# Revit family: НЕВАТОМ_Щит приточно-вытяжной вентиляцией ABUm-PE-1-ZM, Версия 1
name_source: partatom
category: Электрооборудование
revit_build: Autodesk Revit 2017 (Build: 20170118_1100(x64)
units: mm (PartAtom-declared; Revit-internal decimal feet)

## family parameters
Всегда вертикально = Да
Конфигурация панели = Два столбца, слева направо
На основе рабочей плоскости = Нет
Общий = Нет
При загрузке вырезать с полостями = Нет
Размер круглого соединителя = Использовать диаметр
Тип детали = Щит
Точка расчета площади = Нет

## types (26) — shared parameters
ADSK_Единица измерения = шт.
ADSK_Завод-изготовитель = НЕВАТОМ
ADSK_Количество = 1
ADSK_Напряжение = 380 В

## per-type parameters (varying)
| type | ADSK_Размер_Высота | ADSK_Размер_Длина | ADSK_Размер_Ширина | НЕВАТОМ_Количество ступеней нагревателя | НЕВАТОМ_Максимальная мощность нагревателя | НЕВАТОМ_Номинальный ток двигателя | НЕВАТОМ_Ориентировочная мощность двигателя | НЕВАТОМ_Преобразователь частоты Danfoss, кВт |
| ABUm-РE-1-ZM-0,35/0,35-4,5/1 | 800 мм | 680 мм | 200 мм | 1 | 5 кВт | 2 А | 0 кВт | ND-051 0,37 кВт для 3 фазы |
| ABUm-РE-1-ZM-0,75/0,75-4,5/1 | 800 мм | 680 мм | 200 мм | 1 | 5 кВт | 3 А | 1 кВт | ND-051 0,75 кВт для 3 фазы |
| ABUm-РE-1-ZM-0,35/0,35-6/1 | 800 мм | 680 мм | 200 мм | 1 | 6 кВт | 2 А | 0 кВт | ND-051 0,37 кВт для 3 фазы |
| ABUm-РE-1-ZM-0,75/0,75-6/1 | 800 мм | 680 мм | 200 мм | 1 | 6 кВт | 3 А | 1 кВт | ND-051 0,75 кВт для 3 фазы |
| ABUm-РE-1-ZM-0,35/0,35-7,5/1 | 800 мм | 680 мм | 200 мм | 0 | 0 кВт | 0 А | 0 кВт |  |
| ABUm-РE-1-ZM-0,75/0,75-7,5/1 | 800 мм | 680 мм | 200 мм | 1 | 8 кВт | 3 А | 1 кВт | ND-051 0,75 кВт для 3 фазы |
| ABUm-РE-1-ZM-0,35/0,35-12/2 | 800 мм | 680 мм | 200 мм | 2 | 12 кВт | 2 А | 0 кВт | ND-051 0,37 кВт для 3 фазы |
| ABUm-РE-1-ZM-0,75/0,75-12/2 | 800 мм | 680 мм | 200 мм | 2 | 12 кВт | 3 А | 1 кВт | ND-051 0,75 кВт для 3 фазы |
| ABUm-РE-1-ZM-0,35/0,35-15/2 | 800 мм | 680 мм | 200 мм | 0 | 0 кВт | 0 А | 0 кВт | ND-051 0,37 кВт для 3 фазы |
| ABUm-РE-1-ZM-0,75/0,75-15/2 | 800 мм | 680 мм | 200 мм | 0 | 0 кВт | 0 А | 0 кВт | ND-051 0,75 кВт для 3 фазы |
| ABUm-РE-1-ZM-0,75/0,75-22,5/2 | 800 мм | 680 мм | 200 мм | 2 | 23 кВт | 3 А | 1 кВт | ND-051 0,75 кВт для 3 фазы |
| ABUm-РE-1-ZM-1,5/1,5-22,5/2 | 800 мм | 680 мм | 200 мм | 2 | 23 кВт | 4 А | 2 кВт | ND-051 1,5 кВт для 3 фазы |
| ABUm-РE-1-ZM-1,5/1,5-30/2 | 800 мм | 680 мм | 200 мм | 2 | 30 кВт | 4 А | 2 кВт | ND-051 1,5 кВт для 3 фазы |
| ABUm-РE-1-ZM-2,2/2,2-30/2 | 800 мм | 680 мм | 200 мм | 2 | 30 кВт | 6 А | 2 кВт | ND-051 2,2 кВт для 3 фазы |
| ABUm-РE-1-ZM-1,5/1,5-37,5/3 | 800 мм | 680 мм | 200 мм | 3 | 38 кВт | 4 А | 2 кВт | ND-051 1,5 кВт для 3 фазы |
| ABUm-РE-1-ZM-2,2/2,2-37,5/3 | 800 мм | 680 мм | 200 мм | 3 | 38 кВт | 6 А | 2 кВт | ND-051 2,2 кВт для 3 фазы |
| ABUm-РE-1-ZM-2,2/2,2-45/3 | 800 мм | 680 мм | 200 мм | 3 | 45 кВт | 6 А | 2 кВт | ND-051 2,2 кВт для 3 фазы |
| ABUm-РE-1-ZM-4,0/4,0-45/3 | 800 мм | 680 мм | 200 мм | 3 | 0 кВт | 0 А | 0 кВт | ND-051 4,0 кВт для 3 фазы |
| ABUm-РE-1-ZM-4,0/4,0-60/4 | 800 мм | 680 мм | 200 мм | 4 | 60 кВт | 10 А | 4 кВт | ND-051 4,0 кВт для 3 фазы |
| ABUm-РE-1-ZM-4,0/4,0-75/5 | 1000 мм | 880 мм | 300 мм | 5 | 75 кВт | 10 А | 4 кВт | ND-051 4,0 кВт для 3 фазы |
| ABUm-РE-1-ZM-5,5/5,5-75/5 | 1000 мм | 880 мм | 300 мм | 0 | 0 кВт | 0 А | 0 кВт | ND-051 5,5 кВт для 3 фазы |
| ABUm-РE-1-ZM-5,5/5,5-90/5 | 1000 мм | 880 мм | 300 мм | 5 | 90 кВт | 13 А | 6 кВт | ND-051 5,5 кВт для 3 фазы |
| ABUm-РE-1-ZM-7,5/7,5-90/5 | 1000 мм | 880 мм | 300 мм | 5 | 90 кВт | 18 А | 8 кВт | ND-051 7,5 кВт для 3 фазы |
| ABUm-РE-1-ZM-7,5/7,5-120/5 | 1000 мм | 880 мм | 300 мм | 5 | 120 кВт | 18 А | 8 кВт | ND-051 7,5 кВт для 3 фазы |
| ABUm-РE-1-ZM-15/15-120/5 | 1000 мм | 880 мм | 300 мм | 5 | 120 кВт | 32 А | 15 кВт | ND-051 15 кВт для 3 фазы |
| ABUm-РE-1-ZM-5,5/5,5-60/4 | 800 мм | 680 мм | 200 мм | 4 | 60 кВт | 13 А | 6 кВт | ND-051 5,5 кВт для 3 фазы |

note: column(s) folded — value = type name in every type: ADSK_Марка, ADSK_Наименование
